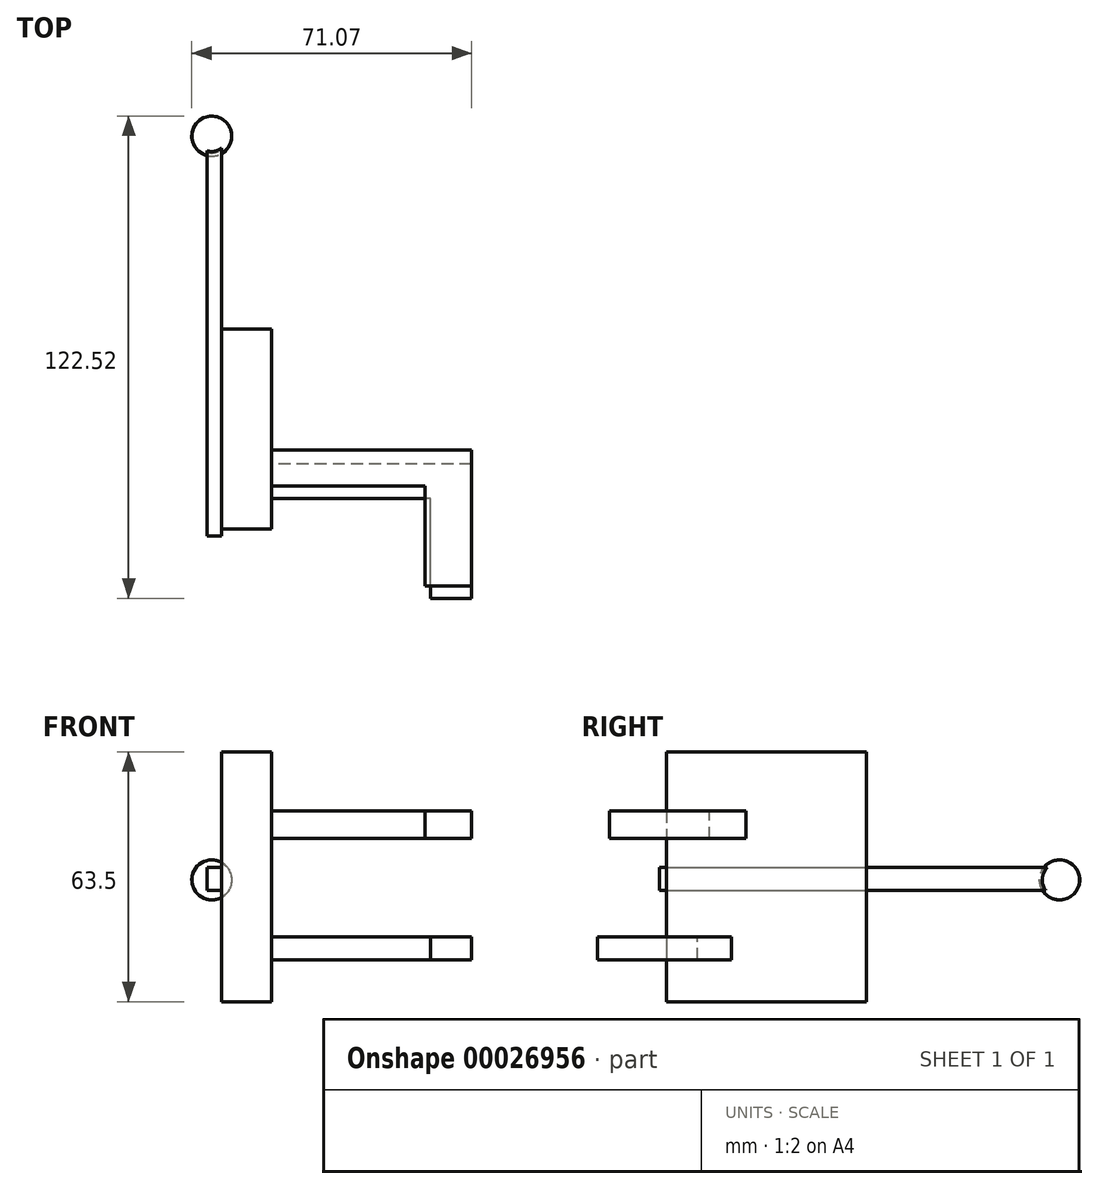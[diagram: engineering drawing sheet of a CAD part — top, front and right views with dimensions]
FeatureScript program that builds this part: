
annotation { "Feature Type Name" : "Feature", "Feature Type Description" : "" }
export const myFeature = defineFeature(function(context is Context, id is Id, definition is map)
    precondition{}
    {
        {
            var Q0;
            Q0=qCreatedBy(makeId("Front.planeOp"),FACE);
            var sketch = newSketch(context, id + "F0", { "sketchPlane" : qUnion([Q0])});
            skArc(sketch, "E0", {"start": v(0, -5) * mm, "mid": v(5.06, 0.08) * mm, "end": v(0, 5.16) * mm});
            skLineSegment(sketch, "E1", {"start": v(0, 5.16) * mm, "end": v(0, -5) * mm});
            skSolve(sketch);
        }
        {
            var Q0;
            Q0=makeQuery(id+"F0.imprint","IMPRINT",FACE,{"disambiguationData":[TD([[makeQuery(id+"F0.imprint","IMPRINT",EDGE,{"derivedFrom":sQuery(id+"F0.wireOp",EDGE,"E0")}),1.0]])]});
            var Q1;
            Q1=sQuery(id+"F0.wireOp",EDGE,"E1");
            revolve(context, id + "F1", {"entities" : qUnion([Q0]), "axis" : qUnion([Q1]), "revolveType" : RevolveType.FULL});
        }
        {
            var Q0;
            Q0=qCreatedBy(makeId("Front.planeOp"),FACE);
            cPlane(context, id + "F2", {"entities" : qUnion([Q0]), "cplaneType" : CPlaneType.OFFSET, "offset" : 5.08 * mm, "width" : 152.4 * mm, "height" : 152.4 * mm});
        }
        {
            var Q0;
            Q0=qCreatedBy(id+"F2.planeOp",FACE);
            var sketch = newSketch(context, id + "F3", { "sketchPlane" : qUnion([Q0])});
            skLineSegment(sketch, "E2.bottom", {"start": v(-1.21, 3.28) * mm, "end": v(2.47, 3.28) * mm});
            skLineSegment(sketch, "E2.top", {"start": v(-1.21, -2.61) * mm, "end": v(2.47, -2.61) * mm});
            skLineSegment(sketch, "E2.left", {"start": v(-1.21, 3.28) * mm, "end": v(-1.21, -2.61) * mm});
            skLineSegment(sketch, "E2.right", {"start": v(2.47, 3.28) * mm, "end": v(2.47, -2.61) * mm});
            skSolve(sketch);
        }
        {
            var Q0;
            Q0=makeQuery(id+"F3.imprint","IMPRINT",FACE,{"disambiguationData":[TD([[makeQuery(id+"F3.imprint","IMPRINT",EDGE,{"derivedFrom":sQuery(id+"F3.wireOp",EDGE,"E2.bottom")}),-1.0]])]});
            extrude(context, id + "F4", {"entities" : qUnion([Q0]), "operationType" : NewBodyOperationType.REMOVE, "oppositeDirection" : true, "depth" : 5.08 * mm});
        }
        {
            var Q0;
            Q0=makeQuery(id+"F4.boolean.opBoolean","COPY",FACE,{"derivedFrom":makeQuery(id+"F4.opExtrude","CAP_FACE",FACE,{"disambiguationData":[OSD([sQuery(id+"F3.wireOp",EDGE,"E2.bottom"),sQuery(id+"F3.wireOp",EDGE,"E2.top"),sQuery(id+"F3.wireOp",EDGE,"E2.left"),sQuery(id+"F3.wireOp",EDGE,"E2.right")])],"isStart":false})});
            extrude(context, id + "F5", {"entities" : qUnion([Q0]), "operationType" : NewBodyOperationType.ADD, "depth" : 101.6 * mm});
        }
        {
            var Q0;
            Q0=makeQuery(id+"F5.opExtrude","SWEPT_FACE",FACE,{"disambiguationData":[OSD([sQuery(id+"F3.wireOp",EDGE,"E2.right")])]});
            var sketch = newSketch(context, id + "F6", { "sketchPlane" : qUnion([Q0])});
            skLineSegment(sketch, "E3.bottom", {"start": v(-99.88, 32.65) * mm, "end": v(-49.08, 32.65) * mm});
            skLineSegment(sketch, "E3.top", {"start": v(-99.88, -30.85) * mm, "end": v(-49.08, -30.85) * mm});
            skLineSegment(sketch, "E3.left", {"start": v(-99.88, 32.65) * mm, "end": v(-99.88, -30.85) * mm});
            skLineSegment(sketch, "E3.right", {"start": v(-49.08, 32.65) * mm, "end": v(-49.08, -30.85) * mm});
            skSolve(sketch);
        }
        {
            var Q0;
            {var subQ5=sQuery(id+"F6.wireOp",EDGE,"E3.bottom");Q0=makeQuery(id+"F6.imprint","IMPRINT",FACE,{"disambiguationData":[TD([[makeQuery(id+"F6.imprint","IMPRINT",EDGE,{"derivedFrom":subQ5}),-1.0]])]});}
            var Q1;
            {var subQ0=sQuery(id+"F3.wireOp",EDGE,"E2.right");var subQ4=sQuery(id+"F6.wireOp",EDGE,"E3.left");var subQ6=makeQuery(id+"F5.opExtrude","SWEPT_EDGE",EDGE,{"disambiguationData":[OSD([sQuery(id+"F3.wireOp",EDGE,"E2.bottom"),subQ0])]});var subQ8=makeQuery(id+"F6.imprint","INTERSECT",VERTEX,{"derivedFrom":[subQ6,subQ4]});Q1=makeQuery(id+"F6.imprint","IMPRINT",FACE,{"disambiguationData":[TD([[makeQuery(id+"F6.imprint","IMPRINT",EDGE,{"disambiguationData":[TD([[subQ8,-1.0]])],"derivedFrom":subQ4}),1.0]])]});}
            var Q2;
            {var subQ5=sQuery(id+"F6.wireOp",EDGE,"E3.top");Q2=makeQuery(id+"F6.imprint","IMPRINT",FACE,{"disambiguationData":[TD([[makeQuery(id+"F6.imprint","IMPRINT",EDGE,{"derivedFrom":subQ5}),1.0]])]});}
            extrude(context, id + "F7", {"entities" : qUnion([Q0, Q1, Q2]), "operationType" : NewBodyOperationType.ADD, "depth" : 12.7 * mm});
        }
        {
            var Q0;
            Q0=makeQuery(id+"F7.opExtrude","CAP_FACE",FACE,{"disambiguationData":[OSD([sQuery(id+"F6.wireOp",EDGE,"E3.bottom"),sQuery(id+"F6.wireOp",EDGE,"E3.top"),sQuery(id+"F6.wireOp",EDGE,"E3.left"),sQuery(id+"F6.wireOp",EDGE,"E3.right")])],"isStart":false});
            var sketch = newSketch(context, id + "F8", { "sketchPlane" : qUnion([Q0])});
            skLineSegment(sketch, "E4.bottom", {"start": v(-92.02, -20.24) * mm, "end": v(-83.32, -20.24) * mm});
            skLineSegment(sketch, "E4.top", {"start": v(-92.02, -14.37) * mm, "end": v(-83.32, -14.37) * mm});
            skLineSegment(sketch, "E4.left", {"start": v(-92.02, -20.24) * mm, "end": v(-92.02, -14.37) * mm});
            skLineSegment(sketch, "E4.right", {"start": v(-83.32, -20.24) * mm, "end": v(-83.32, -14.37) * mm});
            skLineSegment(sketch, "E5.bottom", {"start": v(-88.91, 10.58) * mm, "end": v(-79.75, 10.58) * mm});
            skLineSegment(sketch, "E5.top", {"start": v(-88.91, 17.6) * mm, "end": v(-79.75, 17.6) * mm});
            skLineSegment(sketch, "E5.left", {"start": v(-88.91, 10.58) * mm, "end": v(-88.91, 17.6) * mm});
            skLineSegment(sketch, "E5.right", {"start": v(-79.75, 10.58) * mm, "end": v(-79.75, 17.6) * mm});
            skSolve(sketch);
        }
        {
            var Q0;
            Q0=makeQuery(id+"F8.imprint","IMPRINT",FACE,{"disambiguationData":[TD([[makeQuery(id+"F8.imprint","IMPRINT",EDGE,{"derivedFrom":sQuery(id+"F8.wireOp",EDGE,"E4.bottom")}),1.0]])]});
            var Q1;
            Q1=makeQuery(id+"F8.imprint","IMPRINT",FACE,{"disambiguationData":[TD([[makeQuery(id+"F8.imprint","IMPRINT",EDGE,{"derivedFrom":sQuery(id+"F8.wireOp",EDGE,"E5.bottom")}),1.0]])]});
            extrude(context, id + "F9", {"entities" : qUnion([Q0, Q1]), "operationType" : NewBodyOperationType.ADD, "depth" : 50.8 * mm});
        }
        {
            var Q0;
            Q0=makeQuery(id+"F9.opExtrude","SWEPT_FACE",FACE,{"disambiguationData":[OSD([sQuery(id+"F8.wireOp",EDGE,"E4.left")])]});
            var sketch = newSketch(context, id + "F10", { "sketchPlane" : qUnion([Q0])});
            skLineSegment(sketch, "E6.bottom", {"start": v(55.56, -14.37) * mm, "end": v(65.97, -14.37) * mm});
            skLineSegment(sketch, "E6.top", {"start": v(55.56, -20.24) * mm, "end": v(65.97, -20.24) * mm});
            skLineSegment(sketch, "E6.left", {"start": v(55.56, -14.37) * mm, "end": v(55.56, -20.24) * mm});
            skLineSegment(sketch, "E6.right", {"start": v(65.97, -14.37) * mm, "end": v(65.97, -20.24) * mm});
            skSolve(sketch);
        }
        {
            var Q0;
            Q0=makeQuery(id+"F10.imprint","IMPRINT",FACE,{"disambiguationData":[TD([[makeQuery(id+"F10.imprint","IMPRINT",EDGE,{"derivedFrom":sQuery(id+"F10.wireOp",EDGE,"E6.bottom")}),1.0]])]});
            var Q1;
            Q1=makeQuery(id+"F10.imprint","IMPRINT",FACE,{"disambiguationData":[TD([[makeQuery(id+"F10.imprint","IMPRINT",EDGE,{"derivedFrom":sQuery(id+"F10.wireOp",EDGE,"cacfc5d5-e1f7-45d4-9577-c5ebc7aeeb9b.bottom")}),-1.0]])]});
            extrude(context, id + "F11", {"entities" : qUnion([Q0, Q1]), "operationType" : NewBodyOperationType.ADD, "depth" : 25.4 * mm});
        }
        {
            var Q0;
            Q0=makeQuery(id+"F9.opExtrude","SWEPT_FACE",FACE,{"disambiguationData":[OSD([sQuery(id+"F8.wireOp",EDGE,"E5.left")])]});
            var sketch = newSketch(context, id + "F12", { "sketchPlane" : qUnion([Q0])});
            skLineSegment(sketch, "E7.bottom", {"start": v(54.16, 17.6) * mm, "end": v(65.97, 17.6) * mm});
            skLineSegment(sketch, "E7.top", {"start": v(54.16, 10.58) * mm, "end": v(65.97, 10.58) * mm});
            skLineSegment(sketch, "E7.left", {"start": v(54.16, 17.6) * mm, "end": v(54.16, 10.58) * mm});
            skLineSegment(sketch, "E7.right", {"start": v(65.97, 17.6) * mm, "end": v(65.97, 10.58) * mm});
            skSolve(sketch);
        }
        {
            var Q0;
            Q0=makeQuery(id+"F12.imprint","IMPRINT",FACE,{"disambiguationData":[TD([[makeQuery(id+"F12.imprint","IMPRINT",EDGE,{"derivedFrom":sQuery(id+"F12.wireOp",EDGE,"E7.bottom")}),1.0]])]});
            extrude(context, id + "F13", {"entities" : qUnion([Q0]), "operationType" : NewBodyOperationType.ADD, "depth" : 25.4 * mm});
        }
    });
